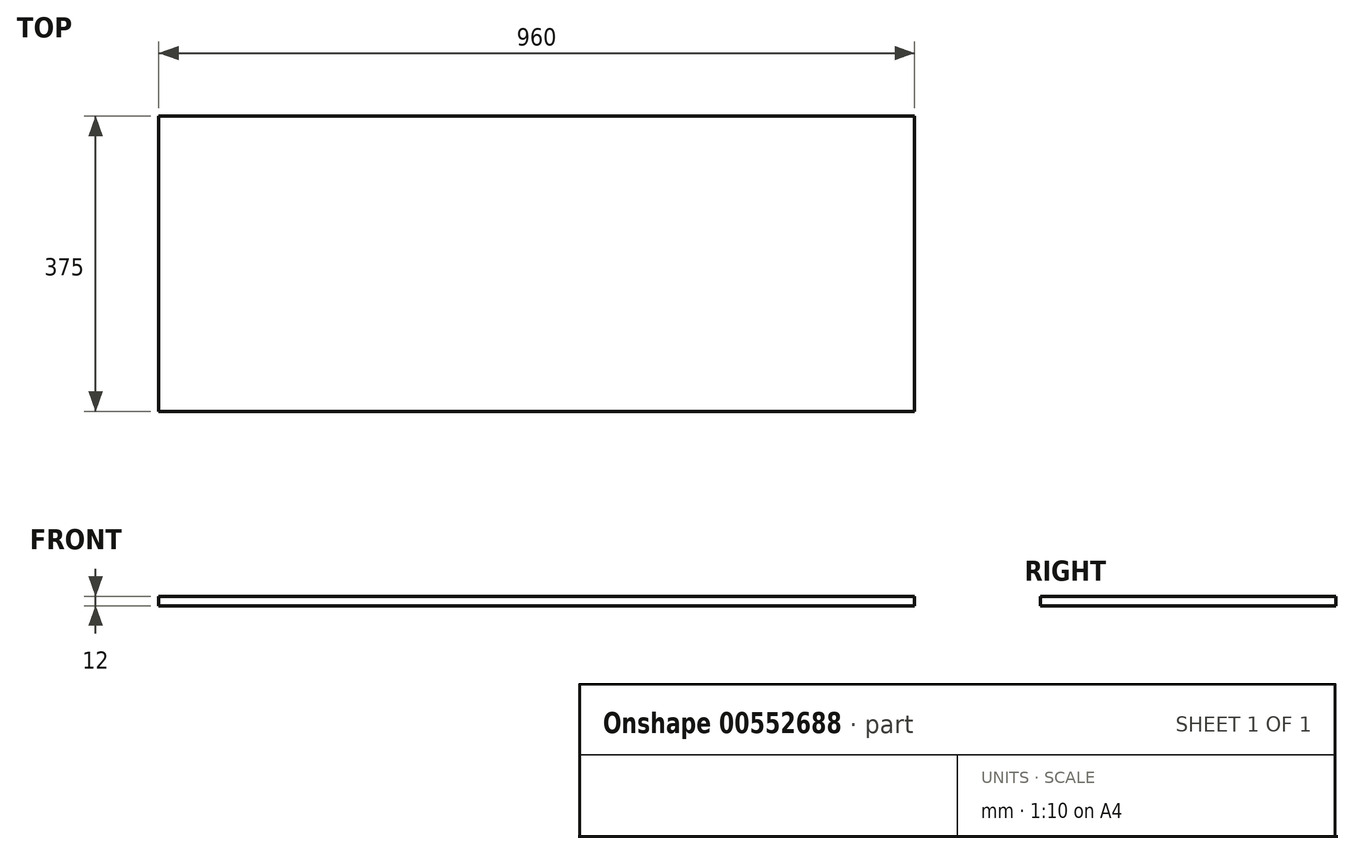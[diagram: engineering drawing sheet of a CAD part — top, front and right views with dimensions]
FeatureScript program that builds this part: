
annotation { "Feature Type Name" : "Feature", "Feature Type Description" : "" }
export const myFeature = defineFeature(function(context is Context, id is Id, definition is map)
    precondition{}
    {
        {
            var Q0;
            Q0=qCreatedBy(makeId("Top.planeOp"),FACE);
            var sketch = newSketch(context, id + "F0", { "sketchPlane" : qUnion([Q0])});
            skLineSegment(sketch, "E0.bottom", {"start": v(480, 187.5) * mm, "end": v(-480, 187.5) * mm});
            skLineSegment(sketch, "E0.top", {"start": v(480, -187.5) * mm, "end": v(-480, -187.5) * mm});
            skLineSegment(sketch, "E0.left", {"start": v(480, 187.5) * mm, "end": v(480, -187.5) * mm});
            skLineSegment(sketch, "E0.right", {"start": v(-480, 187.5) * mm, "end": v(-480, -187.5) * mm});
            skPoint(sketch, "E0.middle", {"position": v(0, 0) * mm});
            skSolve(sketch);
        }
        {
            var Q0;
            Q0 = qSketchRegion(id + "F0", true);
            extrude(context, id + "F1", {"entities" : qUnion([Q0]), "oppositeDirection" : true, "depth" : 12 * mm, "offsetDistance" : 25 * mm});
        }
    });
